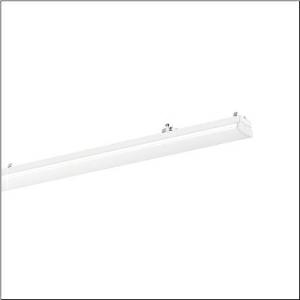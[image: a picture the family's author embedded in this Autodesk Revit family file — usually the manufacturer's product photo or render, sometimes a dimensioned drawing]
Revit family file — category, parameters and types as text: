
# Revit family: licross_11_recessed_opal_mo_51tl1ddn46xg
name_source: partatom
category: Lighting Fixtures
units: mm (PartAtom-declared; Revit-internal decimal feet)

## family parameters
Cut with Voids When Loaded = No
Host = Face
Light Source = No
Part Type = Normal
Room Calculation Point = No
Round Connector Dimension = Use Diameter
Shared = No

## types (1)
- --- (1 x LED, 6320 lm, 35.2 W, 4000K)
    Apparent Load = 35 VA
    CIE Flux Codes = 44 73 91 87 100
    Color Rendering = 80
    Color Temperature = 4000K
    Default Elevation = 1800 mm
    Description = Licross 11 recessed opal MO, luminaire insert, of sheet steel, coil coated, white, length: 1.500mm, width: 76mm, height: 87mm, LED rated luminous flux: 6.320lm, light colour: 840, SDCM (Standard Deviation of Colour Matching)MacAdam ≤ 2 SDCM (initial), control gear: DALI 2, with plug, 5-pole, with phase selection, mains connection: 220..240V, AC, 50/60Hz, rated input power: 35W, internal wiring halogen-free, primary optical cover: cover, of PMMA, light emission: direct with ceiling illumination distribution, primary light characteristic: symmetric, protection rating (complete): IP40, insulation class (complete): insulation class I (protective earthing), certification: CE, ENEC, VDE, UKCA, protection symbol: D if used in an environment without relevant dust loads with corresponding accessories, impact resistance: IK06, permissible ambient temperature for indoor applications: -25..+40°C, corresponds to IFS (International Featured Standards) requirements for safety and quality in the food industry, reducing of maximum allowable ambient temperature of 5°C with ceiling mounting, LABS conformity tested according to VDMA 24364:2018-05, The light source and the operating device comply with the requirements of the Ecodesign Regulation (EU) 2019/2020 and are replaceable in accordance with this regulation, packaging unit: 1 piece
    Height = 83 mm
    Lamp = 1 x LED
    Lamp Light Flux = 6320 lm
    Lamp Power = 35.2 W
    Lamp count = 1
    Length = 1500 mm
    Luminous efficacy = 180 lm/W
    Manufacturer = Siteco
    ModVariant = No
    Model = 51TL1DDN46XG
    Mounting Place = Ceiling
    Mounting Type = Pendant
    Number of Poles = 1
    OnlyDefault = Yes
    Power Factor = 1
    Product Name = Licross 11 recessed opal MO
    Product group = luminaire insert | ceiling pendant
    ProductGroupID = 901
    Protection Class = Protection class I
    Protection Degree = IP 40
    RLX_Detail_Level = 1
    RLX_Emergency_Light_Flux = 0 lm
    RLX_Emergency_Type = 0
    RLX_Emergency_Type_DB = No
    RlxData = <blob elided: 27057 chars, md5=4a75cb4f>
    Socket = socket
    Standby Power = 0 W
    System Light Flux = 6320 lm
    System Power = 35 W
    Type Comments = factory setting: luminous flux: 100 % | dim-lin: 254 | 238 mA
    Type Image = l_1313666.jpg
    URL = http://relux.com
    VarID = @adj_083931
    Voltage = 0 V
    Weight = 0.00 kg
    Width = 76 mm

## geometry (parser evidence)
native form markers: Blend x4, Sweep x13
no freeform markers — native parametric forms only
